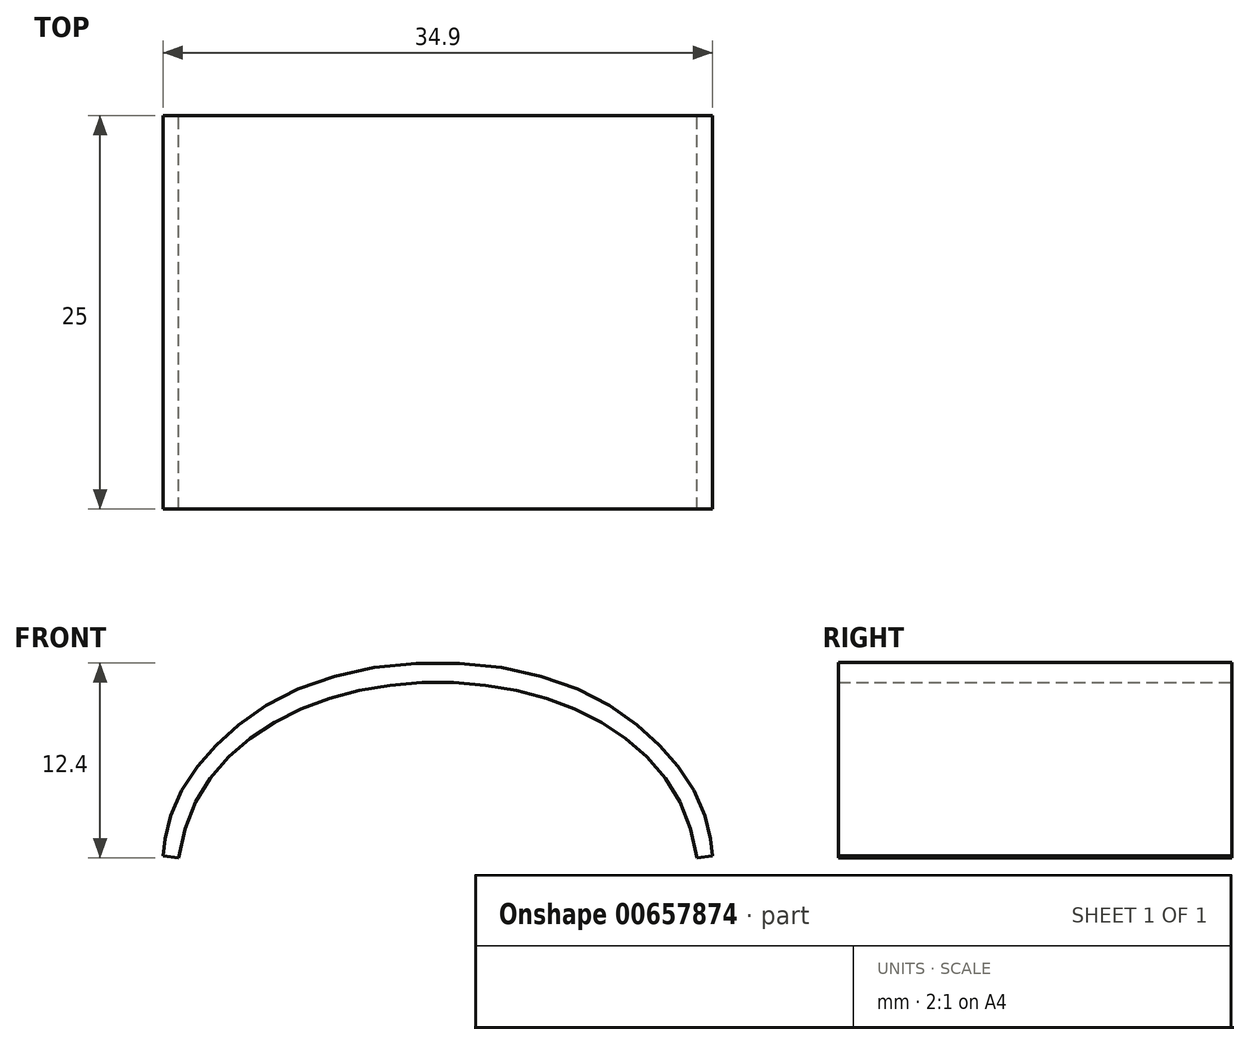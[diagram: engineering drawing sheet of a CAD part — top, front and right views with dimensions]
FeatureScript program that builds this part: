
annotation { "Feature Type Name" : "Feature", "Feature Type Description" : "" }
export const myFeature = defineFeature(function(context is Context, id is Id, definition is map)
    precondition{}
    {
        {
            var Q0;
            Q0=qCreatedBy(makeId("Front.planeOp"),FACE);
            var sketch = newSketch(context, id + "F0", { "sketchPlane" : qUnion([Q0])});
            skFitSpline(sketch, "E0", {"points": [v(-16.46, 0) * mm, v(16.45, 0) * mm], "startDerivative": vector(5.69, 44.64) * mm, "endDerivative": vector(5.64, -44.64) * mm});
            skFitSpline(sketch, "E1.0", {"points": [v(-17.46, 0.13) * mm, v(-17.33, 1.14) * mm, v(-16.84, 3.04) * mm, v(-15.49, 5.53) * mm, v(-13.63, 7.6) * mm, v(-10.6, 9.85) * mm, v(-6.06, 11.68) * mm, v(0, 12.4) * mm, v(6.05, 11.68) * mm, v(10.6, 9.85) * mm, v(13.62, 7.6) * mm, v(15.47, 5.52) * mm, v(16.82, 3.04) * mm, v(17.31, 1.14) * mm, v(17.44, 0.13) * mm]});
            skLineSegment(sketch, "E2", {"start": v(-17.46, 0.13) * mm, "end": v(-16.46, 0) * mm});
            skLineSegment(sketch, "E3", {"start": v(16.45, 0) * mm, "end": v(17.44, 0.13) * mm});
            skSolve(sketch);
        }
        {
            var Q0;
            Q0 = qSketchRegion(id + "F0", true);
            extrude(context, id + "F1", {"entities" : qUnion([Q0]), "depth" : 25 * mm, "offsetDistance" : 25 * mm});
        }
    });
